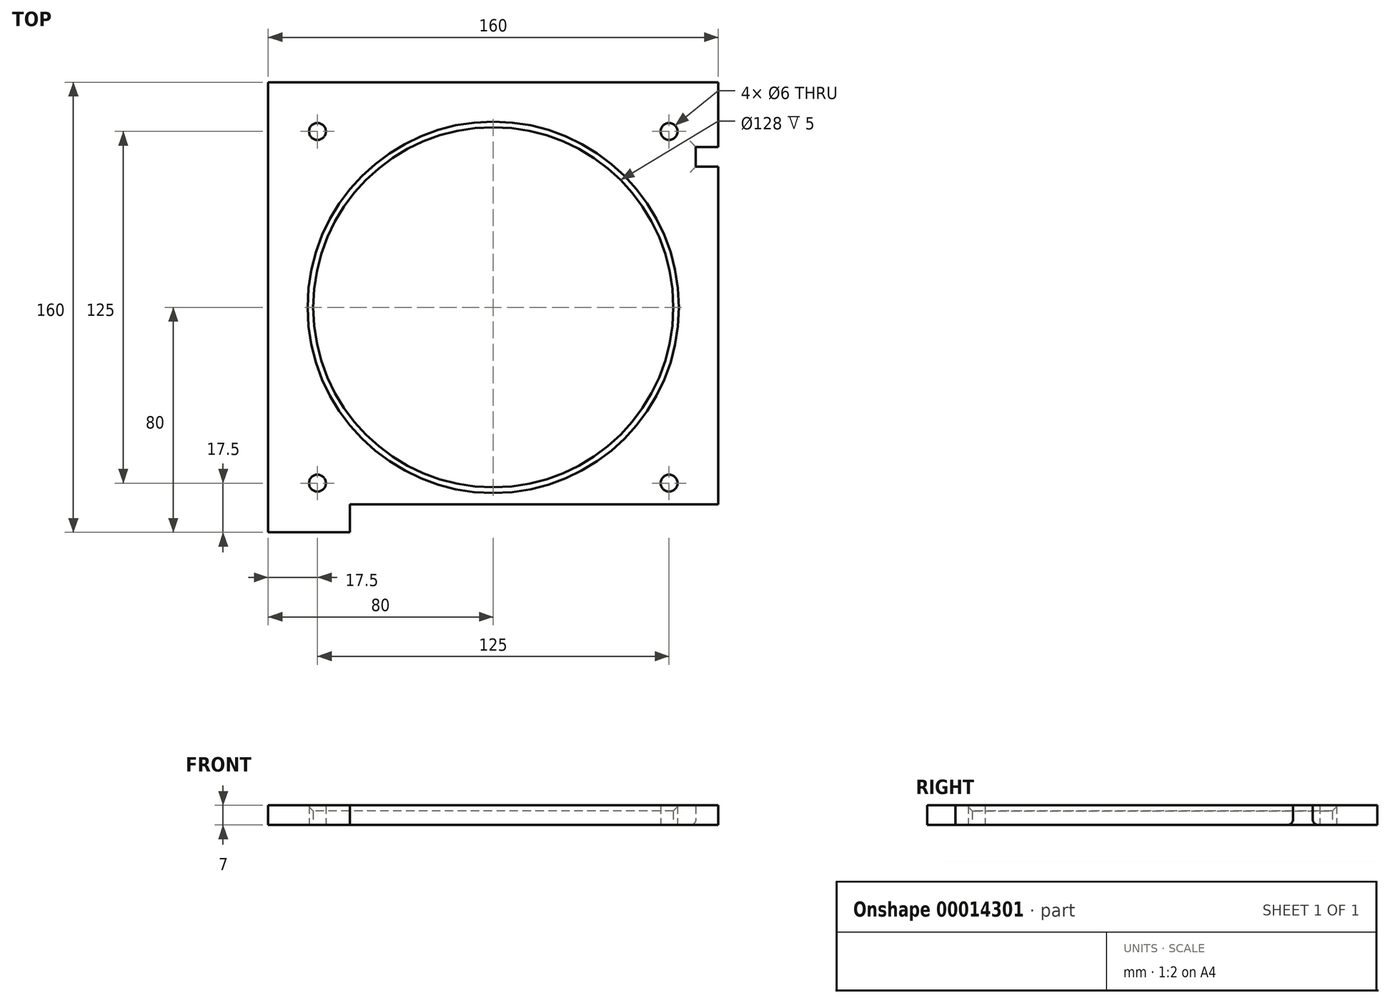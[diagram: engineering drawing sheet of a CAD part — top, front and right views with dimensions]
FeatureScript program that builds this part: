
annotation { "Feature Type Name" : "Feature", "Feature Type Description" : "" }
export const myFeature = defineFeature(function(context is Context, id is Id, definition is map)
    precondition{}
    {
        {
            var Q0;
            Q0=qCreatedBy(makeId("Top.planeOp"),FACE);
            var sketch = newSketch(context, id + "F0", { "sketchPlane" : qUnion([Q0])});
            skLineSegment(sketch, "E0.bottom", {"start": v(-80, 80) * mm, "end": v(80, 80) * mm});
            skLineSegment(sketch, "E0.left", {"start": v(-80, 80) * mm, "end": v(-80, -80) * mm});
            skLineSegment(sketch, "E1", {"start": v(0, 0) * mm, "end": v(-80, 0) * mm, "construction": true});
            skLineSegment(sketch, "E2", {"start": v(0, 0) * mm, "end": v(0, 80) * mm, "construction": true});
            skCircle(sketch, "E3", {"center": v(0, 0) * mm, "radius": 64 * mm});
            skLineSegment(sketch, "E4", {"start": v(-62.5, 62.5) * mm, "end": v(62.5, 62.5) * mm, "construction": true});
            skLineSegment(sketch, "E5", {"start": v(62.5, 62.5) * mm, "end": v(62.5, -62.5) * mm, "construction": true});
            skLineSegment(sketch, "E6", {"start": v(62.5, -62.5) * mm, "end": v(-62.5, -62.5) * mm, "construction": true});
            skLineSegment(sketch, "E7", {"start": v(-62.5, -62.5) * mm, "end": v(-62.5, 62.5) * mm, "construction": true});
            skLineSegment(sketch, "E8", {"start": v(-62.5, 62.5) * mm, "end": v(-80, 62.5) * mm, "construction": true});
            skLineSegment(sketch, "E9", {"start": v(-62.5, 62.5) * mm, "end": v(-62.5, 80) * mm, "construction": true});
            skCircle(sketch, "E10", {"center": v(-62.5, 62.5) * mm, "radius": 3 * mm});
            skCircle(sketch, "E11", {"center": v(-62.5, -62.5) * mm, "radius": 3 * mm});
            skCircle(sketch, "E12", {"center": v(62.5, -62.5) * mm, "radius": 3 * mm});
            skCircle(sketch, "E13", {"center": v(62.5, 62.5) * mm, "radius": 3 * mm});
            skLineSegment(sketch, "E14", {"start": v(-51, -80) * mm, "end": v(-51, -70) * mm});
            skLineSegment(sketch, "E15", {"start": v(-51, -70) * mm, "end": v(80, -70) * mm});
            skLineSegment(sketch, "E16", {"start": v(-80, -80) * mm, "end": v(-51, -80) * mm});
            skLineSegment(sketch, "E17", {"start": v(80, 80) * mm, "end": v(80, 57) * mm});
            skLineSegment(sketch, "E18", {"start": v(80, 57) * mm, "end": v(72, 57) * mm});
            skLineSegment(sketch, "E19", {"start": v(72, 57) * mm, "end": v(72, 50) * mm});
            skLineSegment(sketch, "E20", {"start": v(72, 50) * mm, "end": v(80, 50) * mm});
            skLineSegment(sketch, "E21", {"start": v(80, 50) * mm, "end": v(80, -70) * mm});
            skSolve(sketch);
        }
        {
            var Q0;
            Q0=makeQuery(id+"F0.imprint","IMPRINT",FACE,{"disambiguationData":[TD([[makeQuery(id+"F0.imprint","IMPRINT",EDGE,{"derivedFrom":sQuery(id+"F0.wireOp",EDGE,"E0.bottom")}),-1.0]])]});
            extrude(context, id + "F1", {"entities" : qUnion([Q0]), "depth" : 7 * mm});
        }
        {
            var Q0;
            Q0=makeQuery(id+"F1.opExtrude","CAP_EDGE",EDGE,{"disambiguationData":[OSD([sQuery(id+"F0.wireOp",EDGE,"E3")])],"isStart":false});
            chamfer(context, id + "F2", {"entities" : qUnion([Q0]), "width" : 2 * mm, "tangentPropagation" : true});
        }
        {
            var Q0;
            Q0=makeQuery(id+"F1.opExtrude","CAP_EDGE",EDGE,{"disambiguationData":[OSD([sQuery(id+"F0.wireOp",EDGE,"E20")])],"isStart":true});
            var Q1;
            Q1=makeQuery(id+"F1.opExtrude","CAP_EDGE",EDGE,{"disambiguationData":[OSD([sQuery(id+"F0.wireOp",EDGE,"E19")])],"isStart":true});
            var Q2;
            Q2=makeQuery(id+"F1.opExtrude","CAP_EDGE",EDGE,{"disambiguationData":[OSD([sQuery(id+"F0.wireOp",EDGE,"E18")])],"isStart":true});
            fillet(context, id + "F3", {"entities" : qUnion([Q0, Q1, Q2]), "radius" : 2 * mm, "tangentPropagation" : true, "allowEdgeOverflow" : false});
        }
    });
